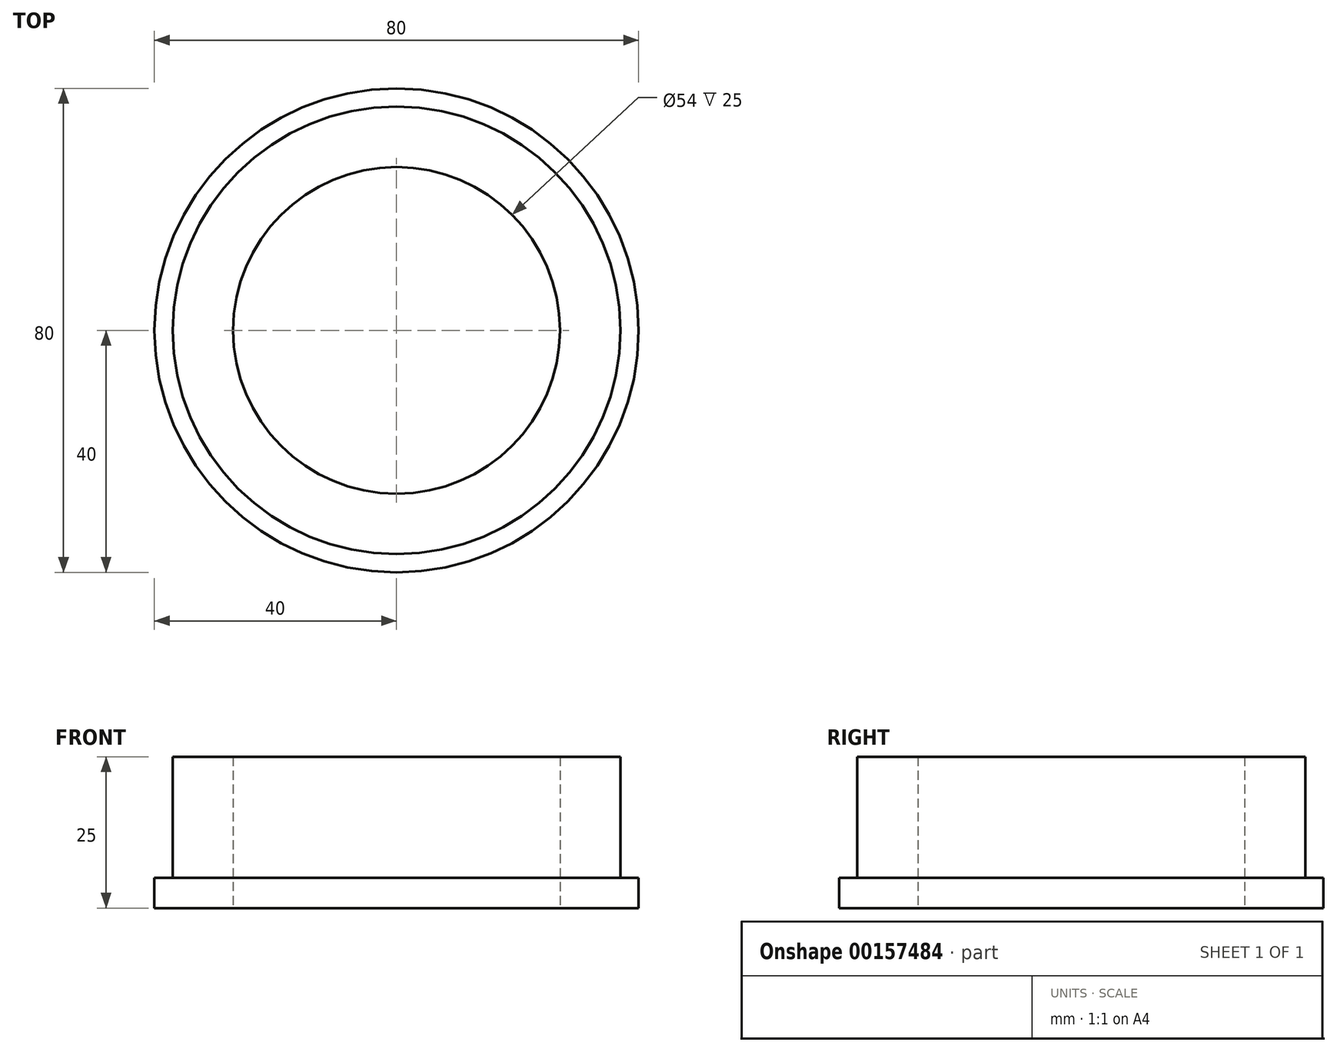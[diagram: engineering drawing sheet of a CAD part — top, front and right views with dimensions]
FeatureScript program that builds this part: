
annotation { "Feature Type Name" : "Feature", "Feature Type Description" : "" }
export const myFeature = defineFeature(function(context is Context, id is Id, definition is map)
    precondition{}
    {
        {
            var Q0;
            Q0=qCreatedBy(makeId("Top.planeOp"),FACE);
            var sketch = newSketch(context, id + "F0", { "sketchPlane" : qUnion([Q0])});
            skCircle(sketch, "E0", {"center": v(0, 0) * mm, "radius": 27 * mm});
            skCircle(sketch, "E1", {"center": v(0, 0) * mm, "radius": 37 * mm});
            skCircle(sketch, "E2", {"center": v(0, 0) * mm, "radius": 40 * mm});
            skSolve(sketch);
        }
        {
            var Q0;
            Q0=makeQuery(id+"F0.imprint","IMPRINT",FACE,{"disambiguationData":[TD([[makeQuery(id+"F0.imprint","IMPRINT",EDGE,{"derivedFrom":sQuery(id+"F0.wireOp",EDGE,"E1")}),-1.0]])]});
            extrude(context, id + "F1", {"entities" : qUnion([Q0]), "depth" : 5 * mm, "offsetDistance" : 25 * mm});
        }
        {
            var Q0;
            Q0=makeQuery(id+"F0.imprint","IMPRINT",FACE,{"disambiguationData":[TD([[makeQuery(id+"F0.imprint","IMPRINT",EDGE,{"derivedFrom":sQuery(id+"F0.wireOp",EDGE,"E0")}),-1.0]])]});
            extrude(context, id + "F2", {"entities" : qUnion([Q0]), "operationType" : NewBodyOperationType.ADD, "depth" : 25 * mm, "offsetDistance" : 25 * mm});
        }
    });
